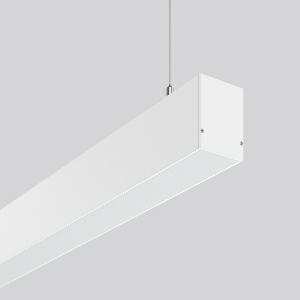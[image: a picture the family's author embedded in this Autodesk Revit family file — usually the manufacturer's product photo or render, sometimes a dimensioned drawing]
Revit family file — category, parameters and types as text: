
# Revit family: less_is_more_50_312319_002_76_020b
name_source: partatom
category: Lighting Fixtures
units: mm (PartAtom-declared; Revit-internal decimal feet)

## family parameters
Cut with Voids When Loaded = No
Host = Face
Light Source = No
Part Type = Normal
Room Calculation Point = No
Round Connector Dimension = Use Diameter
Shared = No

## types (1)
- LESS IS MORE 50 (1 x LED Modul 830, 6150 lm, 3000)
    Apparent Load = 52 VA
    CIE Flux Codes = 49 80 96 63 100
    Color Rendering = 80
    Color Temperature = 3000
    Default Elevation = 1800 mm
    Description = Series: LESS IS MORE 50
Linear pendant luminaire for aesthetically sophisticated lighting. Housing: extruded aluminium profile, powder-coated. End cap aluminium powder-coated. Canopy made of aluminium, powder-coated. Diffuser made of non-yellowing plastic (PMMA), opal. Direct 65%, indirect 35% light emission. Suitable for pendant. 2-point steel cable suspension freely positionable and infinitely height-adjustable. Special lengths available on request. LED unit with integrated converter interchangeable and removable. Suitable for through-wiring. With sensors or as a safety luminaire on request. 
Colour: traffic white, matt (RAL 9016)
Length: 1407 mm
Width: 57 mm
Height: 75 mm
Suspension length: 2000 mm
Lamp: LED
Socket: without socket
Colour temperature: 3000K
Colour rendering index (CRI): 80
Light source: LED
Socket lamp2: Without base
Colour temperature: 3000K
System power: 52 W
Rated luminous flux: 6150 lm
Luminous efficiency: 118 lm/W
Control gear: Converter, dimmable, DALI
Control gear: Converter, dimmable, DALI
Protection class: I
Type of protection: IP 20
    Height = 75 mm
    Lamp = 1 x LED Modul 830
    Lamp Light Flux = 6150 lm
    Lamp count = 1
    Length = 1407 mm
    Lifetime = 50000 h
    Luminous efficacy = 118 lm/W
    Manufacturer = RZB
    ModVariant = No
    Model = 312319.002.76
    Mounting Place = Ceiling
    Mounting Type = Pendant
    Number of Poles = 1
    OnlyDefault = Yes
    Power Factor = 1
    Product Name = LESS IS MORE 50
    Product group = Pendant LED linear luminaires
    ProductGroupID = 907
    Protection Class = Protection class I
    Protection Degree = IP 20
    RLX_Detail_Level = 1
    RLX_Emergency_Light_Flux = 0 lm
    RLX_Emergency_Type = 0
    RLX_Emergency_Type_DB = No
    RlxData = <blob elided: 31597 chars, md5=f4b1e00c>
    Socket = socket
    Standby Power = 0 W
    System Light Flux = 6150 lm
    System Power = 52 W
    Type Comments = Product without accessories
    Type Image = 312318.002.jpg
    URL = http://relux.com
    VarID = ---
    Voltage = 230 V
    Voltage Range = 220-240 V
    Weight = 0.00 kg
    Width = 57 mm

## geometry (parser evidence)
native form markers: Blend x4, Sweep x15
no freeform markers — native parametric forms only
